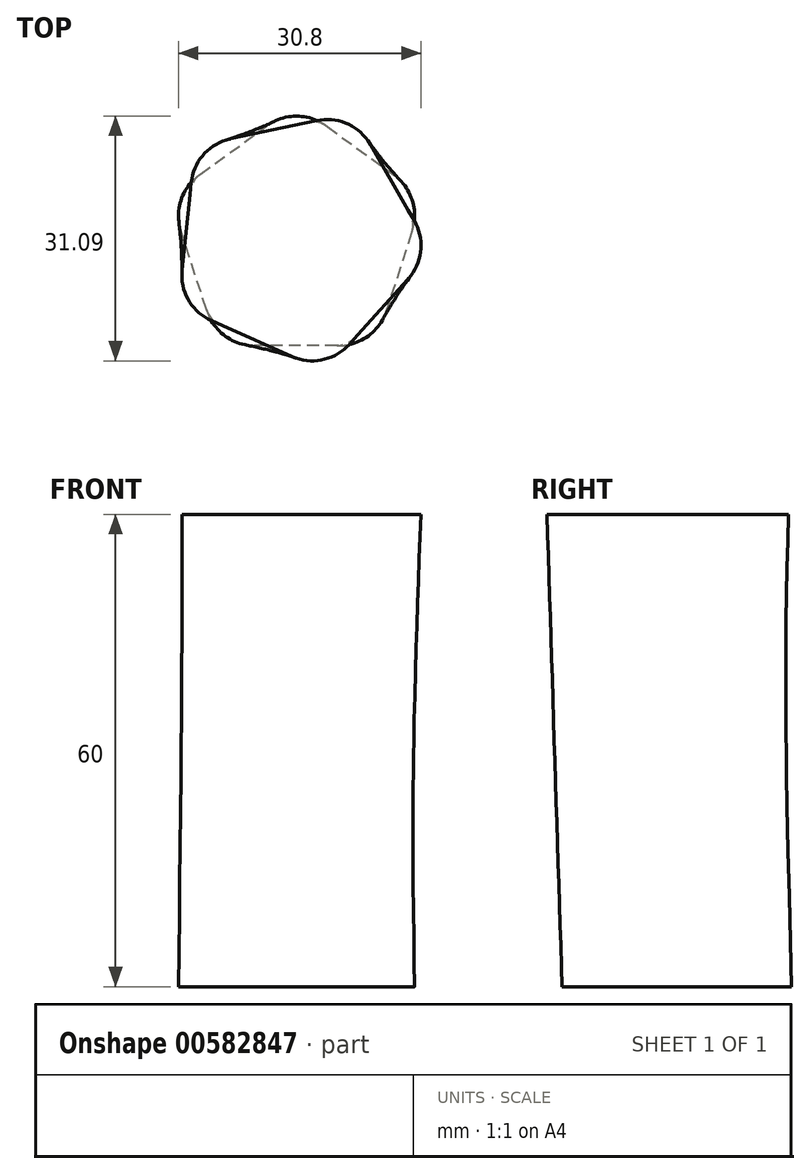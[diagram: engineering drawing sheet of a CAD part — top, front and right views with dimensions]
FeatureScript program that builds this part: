
annotation { "Feature Type Name" : "Feature", "Feature Type Description" : "" }
export const myFeature = defineFeature(function(context is Context, id is Id, definition is map)
    precondition{}
    {
        {
            var Q0;
            Q0=qCreatedBy(makeId("Top.planeOp"),FACE);
            var sketch = newSketch(context, id + "F0", { "sketchPlane" : qUnion([Q0])});
            skCircle(sketch, "E0.cCircle", {"center": v(0, 0) * mm, "radius": 13.7 * mm, "construction": true});
            skLineSegment(sketch, "E0.0", {"start": v(5.35, -13.7) * mm, "end": v(-5.35, -13.7) * mm});
            skLineSegment(sketch, "E0.1", {"start": v(-11.39, -9.32) * mm, "end": v(-14.69, 0.85) * mm});
            skLineSegment(sketch, "E0.2", {"start": v(-12.38, 7.95) * mm, "end": v(-3.73, 14.23) * mm});
            skLineSegment(sketch, "E0.3", {"start": v(3.73, 14.23) * mm, "end": v(12.38, 7.95) * mm});
            skLineSegment(sketch, "E0.4", {"start": v(14.69, 0.85) * mm, "end": v(11.39, -9.32) * mm});
            skPoint(sketch, "E0.0.midPoint", {"position": v(0, -13.7) * mm});
            skPoint(sketch, "E1.visualSharp", {"position": v(-16.11, 5.24) * mm});
            skArc(sketch, "E1.filletArc", {"start": v(-12.38, 7.95) * mm, "mid": v(-14.69, 4.77) * mm, "end": v(-14.69, 0.85) * mm});
            skPoint(sketch, "E2.visualSharp", {"position": v(0, 16.94) * mm});
            skArc(sketch, "E2.filletArc", {"start": v(3.73, 14.23) * mm, "mid": v(0, 15.45) * mm, "end": v(-3.73, 14.23) * mm});
            skPoint(sketch, "E3.visualSharp", {"position": v(16.11, 5.24) * mm});
            skArc(sketch, "E3.filletArc", {"start": v(14.69, 0.85) * mm, "mid": v(14.69, 4.77) * mm, "end": v(12.38, 7.95) * mm});
            skPoint(sketch, "E4.visualSharp", {"position": v(9.96, -13.7) * mm});
            skArc(sketch, "E4.filletArc", {"start": v(5.35, -13.7) * mm, "mid": v(9.08, -12.5) * mm, "end": v(11.39, -9.32) * mm});
            skPoint(sketch, "E5.visualSharp", {"position": v(-9.96, -13.7) * mm});
            skArc(sketch, "E5.filletArc", {"start": v(-11.39, -9.32) * mm, "mid": v(-9.08, -12.5) * mm, "end": v(-5.35, -13.7) * mm});
            skSolve(sketch);
        }
        {
            var Q0;
            Q0=qCreatedBy(makeId("Top.planeOp"),FACE);
            cPlane(context, id + "F1", {"entities" : qUnion([Q0]), "cplaneType" : CPlaneType.OFFSET, "offset" : 60 * mm, "width" : 152.4 * mm, "height" : 152.4 * mm});
        }
        {
            var Q0;
            Q0=qCreatedBy(id+"F1.planeOp",FACE);
            var sketch = newSketch(context, id + "F2", { "sketchPlane" : qUnion([Q0])});
            skCircle(sketch, "E6.cCircle", {"center": v(0, 0) * mm, "radius": 14.04 * mm, "construction": true});
            skLineSegment(sketch, "E6.0", {"start": v(14.17, -5.24) * mm, "end": v(6.7, -13.54) * mm});
            skLineSegment(sketch, "E6.1", {"start": v(-0.6, -15.1) * mm, "end": v(-10.81, -10.55) * mm});
            skLineSegment(sketch, "E6.2", {"start": v(-14.54, -4.08) * mm, "end": v(-13.37, 7.02) * mm});
            skLineSegment(sketch, "E6.3", {"start": v(-8.38, 12.57) * mm, "end": v(2.55, 14.89) * mm});
            skLineSegment(sketch, "E6.4", {"start": v(9.36, 11.85) * mm, "end": v(14.95, 2.18) * mm});
            skPoint(sketch, "E6.0.midPoint", {"position": v(10.43, -9.4) * mm});
            skPoint(sketch, "E7.visualSharp", {"position": v(-12.9, 11.61) * mm});
            skArc(sketch, "E7.filletArc", {"start": v(-8.38, 12.57) * mm, "mid": v(-11.78, 10.6) * mm, "end": v(-13.37, 7.02) * mm});
            skPoint(sketch, "E8.visualSharp", {"position": v(-15.03, -8.67) * mm});
            skArc(sketch, "E8.filletArc", {"start": v(-14.54, -4.08) * mm, "mid": v(-13.73, -7.92) * mm, "end": v(-10.81, -10.55) * mm});
            skPoint(sketch, "E9.visualSharp", {"position": v(3.6, -16.97) * mm});
            skArc(sketch, "E9.filletArc", {"start": v(-0.6, -15.1) * mm, "mid": v(3.3, -15.5) * mm, "end": v(6.7, -13.54) * mm});
            skPoint(sketch, "E10.visualSharp", {"position": v(17.25, -1.82) * mm});
            skArc(sketch, "E10.filletArc", {"start": v(14.17, -5.24) * mm, "mid": v(15.76, -1.66) * mm, "end": v(14.95, 2.18) * mm});
            skPoint(sketch, "E11.visualSharp", {"position": v(7.06, 15.85) * mm});
            skArc(sketch, "E11.filletArc", {"start": v(9.36, 11.85) * mm, "mid": v(6.45, 14.48) * mm, "end": v(2.55, 14.89) * mm});
            skSolve(sketch);
        }
        {
            var Q0;
            Q0 = qSketchRegion(id + "F0", true);
            var Q1;
            Q1 = qSketchRegion(id + "F2", true);
            loft(context, id + "F3", {"sheetProfilesArray" : [{ "sheetProfileEntities" : qUnion([Q0]) }, { "sheetProfileEntities" : qUnion([Q1]) }]});
        }
        {
            var Q0;
            Q0=qCreatedBy(makeId("Front.planeOp"),FACE);
            var sketch = newSketch(context, id + "F4", { "sketchPlane" : qUnion([Q0])});
            skLineSegment(sketch, "E12", {"start": v(0, 0) * mm, "end": v(0, 60) * mm});
            skSolve(sketch);
        }
    });
